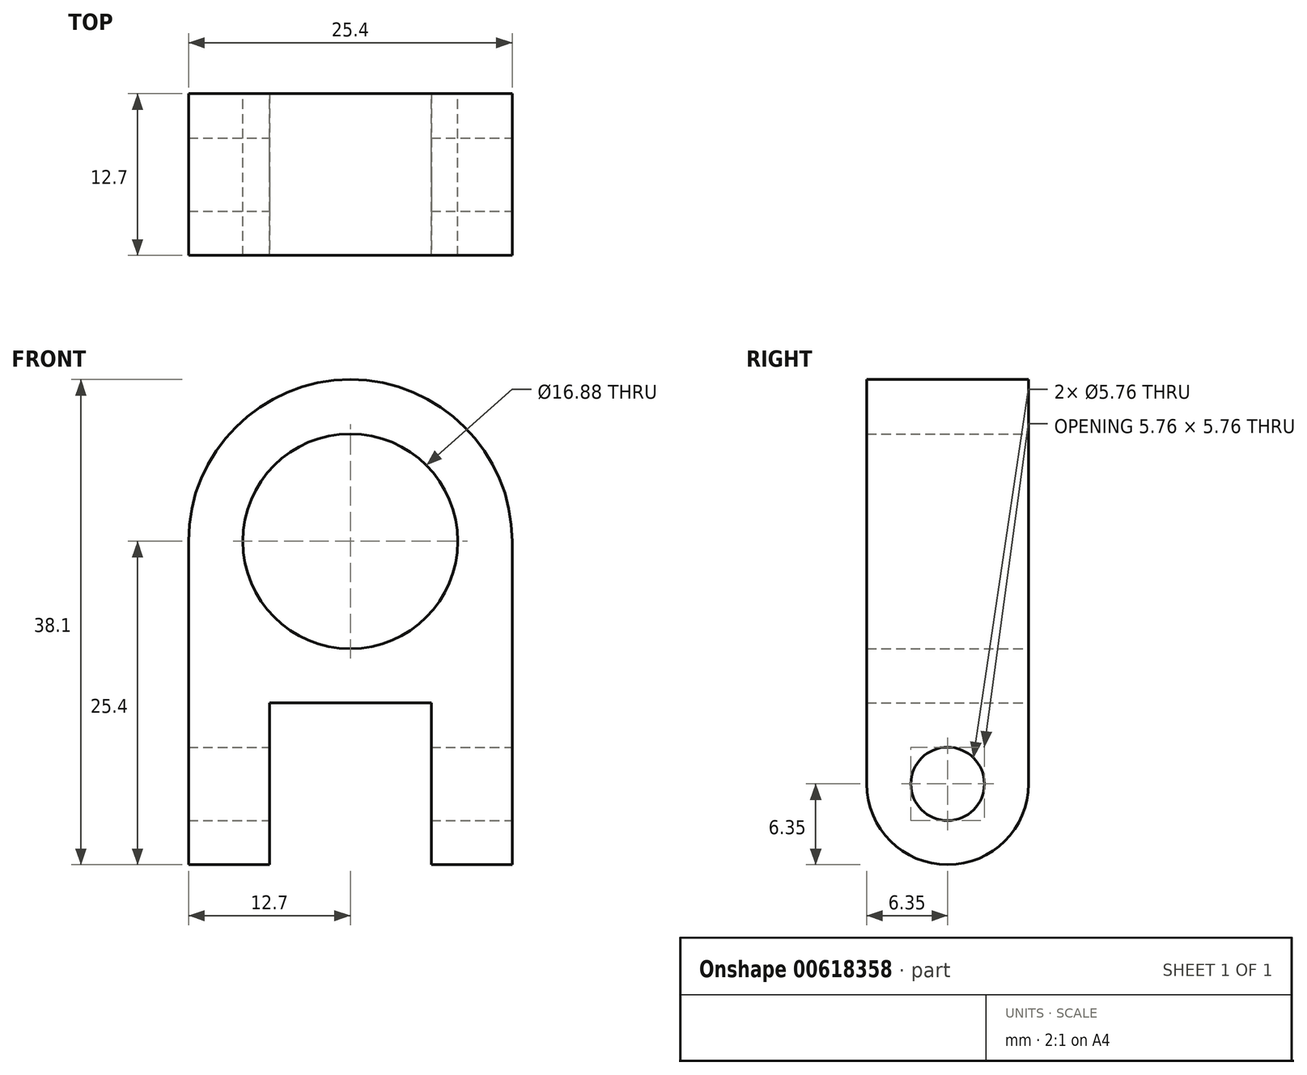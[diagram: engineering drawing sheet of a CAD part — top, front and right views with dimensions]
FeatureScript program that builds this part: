
annotation { "Feature Type Name" : "Feature", "Feature Type Description" : "" }
export const myFeature = defineFeature(function(context is Context, id is Id, definition is map)
    precondition{}
    {
        {
            var Q0;
            Q0=qCreatedBy(makeId("Front.planeOp"),FACE);
            var sketch = newSketch(context, id + "F0", { "sketchPlane" : qUnion([Q0])});
            skCircle(sketch, "E0", {"center": v(0, 0) * mm, "radius": 8.44 * mm});
            skCircle(sketch, "E1", {"center": v(0, 0) * mm, "radius": 12.7 * mm});
            skLineSegment(sketch, "E2", {"start": v(-12.7, 0) * mm, "end": v(-12.7, -25.4) * mm});
            skLineSegment(sketch, "E3", {"start": v(-12.7, -25.4) * mm, "end": v(0, -25.4) * mm});
            skLineSegment(sketch, "E4", {"start": v(0, -25.4) * mm, "end": v(0, -12.7) * mm, "construction": true});
            skLineSegment(sketch, "E5.MirrorCS", {"start": v(12.7, -25.4) * mm, "end": v(0, -25.4) * mm});
            skLineSegment(sketch, "E6.MirrorCS", {"start": v(12.7, 0) * mm, "end": v(12.7, -25.4) * mm});
            skLineSegment(sketch, "E7", {"start": v(-6.35, -25.4) * mm, "end": v(-6.35, -12.7) * mm});
            skLineSegment(sketch, "E8", {"start": v(-6.35, -12.7) * mm, "end": v(0, -12.7) * mm});
            skLineSegment(sketch, "E9.MirrorCS", {"start": v(6.35, -12.7) * mm, "end": v(0, -12.7) * mm});
            skLineSegment(sketch, "E10.MirrorCS", {"start": v(6.35, -25.4) * mm, "end": v(6.35, -12.7) * mm});
            skSolve(sketch);
        }
        {
            var Q0;
            {var subQ2=sQuery(id+"F0.wireOp",EDGE,"E2");Q0=makeQuery(id+"F0.imprint","IMPRINT",FACE,{"disambiguationData":[TD([[makeQuery(id+"F0.imprint","IMPRINT",EDGE,{"derivedFrom":subQ2}),1.0]])]});}
            var Q1;
            {var subQ0=sQuery(id+"F0.wireOp",EDGE,"E6.MirrorCS");Q1=makeQuery(id+"F0.imprint","IMPRINT",FACE,{"disambiguationData":[TD([[makeQuery(id+"F0.imprint","IMPRINT",EDGE,{"derivedFrom":subQ0}),-1.0]])]});}
            var Q2;
            Q2=makeQuery(id+"F0.imprint","IMPRINT",FACE,{"disambiguationData":[TD([[makeQuery(id+"F0.imprint","IMPRINT",EDGE,{"derivedFrom":sQuery(id+"F0.wireOp",EDGE,"E0")}),-1.0]])]});
            extrude(context, id + "F1", {"entities" : qUnion([Q0, Q1, Q2]), "depth" : 12.7 * mm, "offsetDistance" : 25.4 * mm});
        }
        {
            var Q0;
            Q0=makeQuery(id+"F1.opExtrude","CAP_EDGE",EDGE,{"disambiguationData":[OSD([sQuery(id+"F0.wireOp",EDGE,"E3")])],"isStart":false});
            var Q1;
            Q1=makeQuery(id+"F1.opExtrude","CAP_EDGE",EDGE,{"disambiguationData":[OSD([sQuery(id+"F0.wireOp",EDGE,"E3")])],"isStart":true});
            var Q2;
            Q2=makeQuery(id+"F1.opExtrude","CAP_EDGE",EDGE,{"disambiguationData":[OSD([sQuery(id+"F0.wireOp",EDGE,"E5.MirrorCS")])],"isStart":false});
            var Q3;
            Q3=makeQuery(id+"F1.opExtrude","CAP_EDGE",EDGE,{"disambiguationData":[OSD([sQuery(id+"F0.wireOp",EDGE,"E5.MirrorCS")])],"isStart":true});
            fillet(context, id + "F2", {"entities" : qUnion([Q0, Q1, Q2, Q3]), "tangentPropagation" : true, "radius" : 6.35 * mm, "defaultsChanged" : true, "vertexSettings" : [], "allowEdgeOverflow" : false});
        }
        {
            var Q0;
            Q0=makeQuery(id+"F1.opExtrude","SWEPT_FACE",FACE,{"disambiguationData":[OSD([sQuery(id+"F0.wireOp",EDGE,"E6.MirrorCS")])]});
            var sketch = newSketch(context, id + "F3", { "sketchPlane" : qUnion([Q0])});
            skCircle(sketch, "E11", {"center": v(-6.35, -19.05) * mm, "radius": 2.88 * mm});
            skSolve(sketch);
        }
        {
            var Q0;
            Q0 = qSketchRegion(id + "F3", true);
            extrude(context, id + "F4", {"entities" : qUnion([Q0]), "operationType" : NewBodyOperationType.REMOVE, "endBound" : BoundingType.THROUGH_ALL, "oppositeDirection" : true, "depth" : 25.4 * mm, "offsetDistance" : 25.4 * mm});
        }
    });
